# Revit family: KingswayGroup_UncntrlldDrClsr_RecessedSideCloser
name_source: partatom
category: Specialty Equipment
units: mm (PartAtom-declared; Revit-internal decimal feet)

## family parameters
Always vertical = No
Cut with Voids When Loaded = No
Part Type = Normal
Room Calculation Point = No
Round Connector Dimension = Use Diameter
Shared = No
Work Plane-Based = No

## types (1)
- KingswayGroup_UncntrlldDrClsr_RecessedSideCloser
    AssetType = Fixed
    BIMObjectName = KingswayGroup_UncontrolledDoorCloser_RecessedSideCloser
    Category = Pr_30_36_59_92:Uncontrolled door closer
    CloserMaterial = NBS_Concept
    Color = For full range of available finishes and colours, contact Kingsway Group
    Default Elevation = 0 mm  [stored 0 ft]
    Description = Recessed Door Closer
    DurationUnit = year
    Features = A recessed side closer unit that is fully concealed when closed and has an adjustable closing speed and latching action, designed for single-action doors up to 940mm wide and up to 80kg in weight with a maximum opening of 105 degrees.
    Finish = For full range of available finishes and colours, contact Kingsway Group
    IfcExportAs = IfcDiscreteAccessoryType
    IfcExportType = USERDEFINED
    Manufacturer = Kingsway Group
    ManufacturerName = Kingsway Group
    ManufacturerURL = https://kingswaygroupglobal.com
    Material = For full range of available material, contact Kingsway Group
    Model = KG21
    ModelNumber = KG21
    ModelReference = Recessed Side Closer
    Name = UncontrolledDoorCloser_RecessedSideCloser_KG21_KingswayGroup
    NominalHeight = 140 mm  [stored 0.459318 ft]
    NominalLength = 208 mm
    NominalWidth = 28 mm  [stored 0.0918635 ft]
    ProductInformation = https://kingswaygroupglobal.com
    Size = 208 x 140 x 28 mm
    URL = https://kingswaygroupglobal.com
    Uniclass2015Code = Pr_30_36_59_92
    Uniclass2015Title = Uncontrolled door closer
    Uniclass2015Version = Products v1.36
    Version = 1
    WarrantyDescription = 5-Year Guarantee *For faulty manufacture and not for damage
    WarrantyDurationParts = 5
    WarrantyDurationUnit = year

note: [stored X ft] marks values corroborated as IEEE doubles in the binary element streams (Revit-internal decimal feet)

## geometry (parser evidence)
native form markers: Sweep x2
no freeform markers — native parametric forms only
